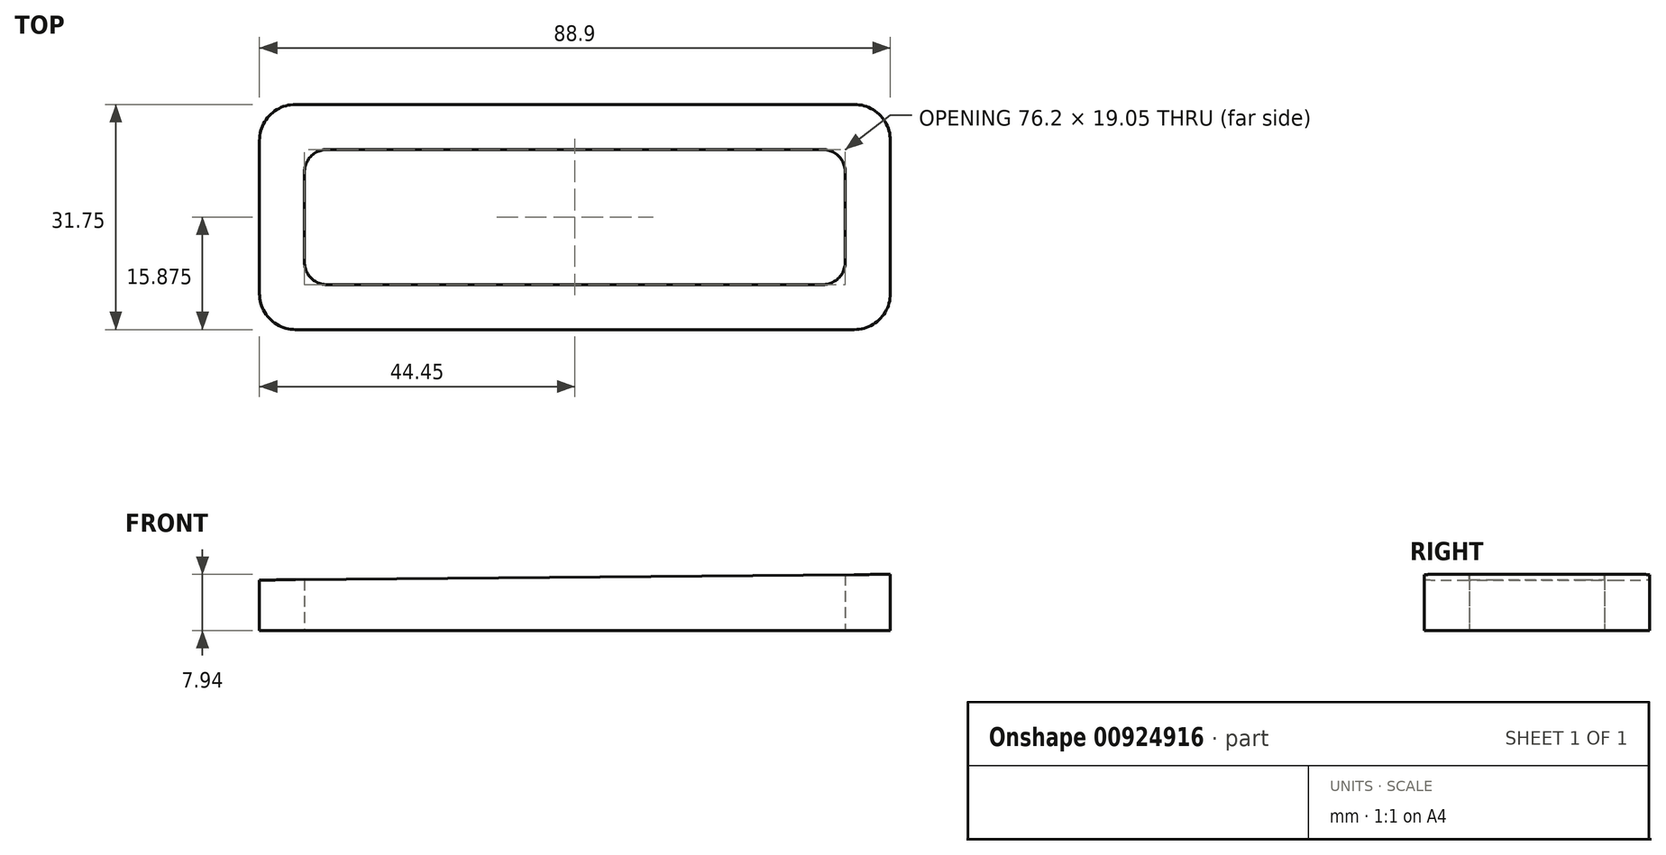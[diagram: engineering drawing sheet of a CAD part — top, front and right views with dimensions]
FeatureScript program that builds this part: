
annotation { "Feature Type Name" : "Feature", "Feature Type Description" : "" }
export const myFeature = defineFeature(function(context is Context, id is Id, definition is map)
    precondition{}
    {
        {
            var Q0;
            Q0=qCreatedBy(makeId("Front.planeOp"),FACE);
            var sketch = newSketch(context, id + "F0", { "sketchPlane" : qUnion([Q0])});
            skLineSegment(sketch, "E0", {"start": v(0, 0) * mm, "end": v(0, 2.38) * mm});
            skLineSegment(sketch, "E1", {"start": v(0, 2.38) * mm, "end": v(609.6, 7.94) * mm});
            skLineSegment(sketch, "E2", {"start": v(609.6, 7.94) * mm, "end": v(609.6, 0) * mm});
            skLineSegment(sketch, "E3", {"start": v(609.6, 0) * mm, "end": v(0, 0) * mm});
            skSolve(sketch);
        }
        {
            var Q0;
            Q0=qCreatedBy(makeId("Front.planeOp"),FACE);
            var sketch = newSketch(context, id + "F1", { "sketchPlane" : qUnion([Q0])});
            skLineSegment(sketch, "E4", {"start": v(609.6, 7.94) * mm, "end": v(520.7, 7.13) * mm});
            skLineSegment(sketch, "E5", {"start": v(520.7, 7.13) * mm, "end": v(520.7, 0) * mm});
            skLineSegment(sketch, "E6", {"start": v(520.7, 0) * mm, "end": v(609.6, 0) * mm});
            skLineSegment(sketch, "E7", {"start": v(609.6, 0) * mm, "end": v(609.6, 7.94) * mm});
            skSolve(sketch);
        }
        {
            var Q0;
            Q0=qCreatedBy(makeId("Front.planeOp"),FACE);
            var sketch = newSketch(context, id + "F2", { "sketchPlane" : qUnion([Q0])});
            skLineSegment(sketch, "E8", {"start": v(444.5, 6.43) * mm, "end": v(444.5, 0) * mm});
            skLineSegment(sketch, "E9", {"start": v(444.5, 0) * mm, "end": v(355.6, 0) * mm});
            skLineSegment(sketch, "E10", {"start": v(-261.26, 0) * mm, "end": v(-261.26, 0) * mm});
            skLineSegment(sketch, "E11", {"start": v(355.55, 5.62) * mm, "end": v(444.5, 6.43) * mm});
            skLineSegment(sketch, "E12", {"start": v(355.55, 5.62) * mm, "end": v(355.6, 0) * mm});
            skSolve(sketch);
        }
        {
            var Q0;
            Q0=qSketchRegion(id+"F1",true);
            extrude(context, id + "F3", {"entities" : qUnion([Q0]), "depth" : 31.75 * mm, "offsetDistance" : 25.4 * mm});
        }
        {
            var Q0;
            Q0=makeQuery(id+"F3.opExtrude","SWEPT_FACE",FACE,{"disambiguationData":[OSD([sQuery(id+"F1.wireOp",EDGE,"E6")])]});
            var sketch = newSketch(context, id + "F4", { "sketchPlane" : qUnion([Q0])});
            skLineSegment(sketch, "E13.bottom", {"start": v(530.23, 25.4) * mm, "end": v(600.08, 25.4) * mm});
            skLineSegment(sketch, "E13.top", {"start": v(530.23, 6.35) * mm, "end": v(600.08, 6.35) * mm});
            skLineSegment(sketch, "E13.left", {"start": v(527.05, 22.22) * mm, "end": v(527.05, 9.52) * mm});
            skLineSegment(sketch, "E13.right", {"start": v(603.25, 22.23) * mm, "end": v(603.25, 9.53) * mm});
            skPoint(sketch, "E14.visualSharp", {"position": v(527.05, 25.4) * mm});
            skArc(sketch, "E14.filletArc", {"start": v(530.23, 25.4) * mm, "mid": v(527.98, 24.47) * mm, "end": v(527.05, 22.22) * mm});
            skPoint(sketch, "E15.visualSharp", {"position": v(527.05, 6.35) * mm});
            skArc(sketch, "E15.filletArc", {"start": v(527.05, 9.52) * mm, "mid": v(527.98, 7.28) * mm, "end": v(530.23, 6.35) * mm});
            skPoint(sketch, "E16.visualSharp", {"position": v(603.25, 6.35) * mm});
            skArc(sketch, "E16.filletArc", {"start": v(600.08, 6.35) * mm, "mid": v(602.32, 7.28) * mm, "end": v(603.25, 9.53) * mm});
            skPoint(sketch, "E17.visualSharp", {"position": v(603.25, 25.4) * mm});
            skArc(sketch, "E17.filletArc", {"start": v(603.25, 22.23) * mm, "mid": v(602.32, 24.47) * mm, "end": v(600.08, 25.4) * mm});
            skSolve(sketch);
        }
        {
            var Q0;
            Q0=qSketchRegion(id+"F4",true);
            extrude(context, id + "F5", {"entities" : qUnion([Q0]), "operationType" : NewBodyOperationType.REMOVE, "endBound" : BoundingType.THROUGH_ALL, "oppositeDirection" : true, "depth" : 25.4 * mm, "offsetDistance" : 25.4 * mm});
        }
        {
            var Q0;
            Q0=makeQuery(id+"F3.opExtrude","CAP_EDGE",EDGE,{"disambiguationData":[OSD([sQuery(id+"F1.wireOp",EDGE,"E5")])],"isStart":false});
            var Q1;
            Q1=makeQuery(id+"F3.opExtrude","CAP_EDGE",EDGE,{"disambiguationData":[OSD([sQuery(id+"F1.wireOp",EDGE,"E5")])],"isStart":true});
            var Q2;
            Q2=makeQuery(id+"F3.opExtrude","CAP_EDGE",EDGE,{"disambiguationData":[OSD([sQuery(id+"F1.wireOp",EDGE,"E7")])],"isStart":false});
            var Q3;
            Q3=makeQuery(id+"F3.opExtrude","CAP_EDGE",EDGE,{"disambiguationData":[OSD([sQuery(id+"F1.wireOp",EDGE,"E7")])],"isStart":true});
            fillet(context, id + "F6", {"entities" : qUnion([Q0, Q1, Q2, Q3]), "radius" : 5.08 * mm, "tangentPropagation" : true, "allowEdgeOverflow" : false});
        }
    });
